FCSTD DOCUMENT  (FreeCAD 0.14R3703 (Git))
Label: hullsSt
License: CC-BY 3.0
LicenseURL: http://creativecommons.org/licenses/by/3.0/
objects: Sketcher::SketchObject×7
note: 7 computed .brp shape members not serialized (recipe doc carries the construction recipe); baked Part::Feature solids carry a one-line shape summary decoded from their .brp

FEATURE [Sketcher::SketchObject] Sketch  label="stemline"
  Placement = pos=(0,0,0) rot=(0.57735,0.57735,0.57735;2.0944rad)
  sketch-geometry (3):
    g0: LineSegment StartX=0 StartY=0 StartZ=0 EndX=25.8227 EndY=11.1446 EndZ=0
    g1: LineSegment StartX=25.8227 StartY=11.1446 StartZ=0 EndX=44.3064 EndY=29.9 EndZ=0
    g2: LineSegment StartX=44.3064 StartY=29.9 StartZ=0 EndX=51.3737 EndY=60.6155 EndZ=0
  constraints (2):
    c: Coincident(g0,g1)
    c: Coincident(g1,g2)
FEATURE [Sketcher::SketchObject] Sketch001  label="cs1"
  Placement = pos=(0,0,0) rot=(1,0,0;1.5708rad)
  sketch-geometry (3):
    g0: LineSegment StartX=0 StartY=0 StartZ=0 EndX=25.0073 EndY=8.15455 EndZ=0
    g1: LineSegment StartX=25.0073 StartY=8.15455 StartZ=0 EndX=38.3264 EndY=24.1918 EndZ=0
    g2: LineSegment StartX=38.3264 StartY=24.1918 StartZ=0 EndX=44.3064 EndY=47.2964 EndZ=0
  constraints (2):
    c: Coincident(g0,g1)
    c: Coincident(g1,g2)
FEATURE [Sketcher::SketchObject] Sketch002  label="cs2"
  Placement = pos=(0,-20,0) rot=(1,0,0;1.5708rad)
  sketch-geometry (3):
    g0: LineSegment StartX=0 StartY=0 StartZ=0 EndX=25.0073 EndY=8.15455 EndZ=0
    g1: LineSegment StartX=25.0073 StartY=8.15455 StartZ=0 EndX=38.3264 EndY=24.1918 EndZ=0
    g2: LineSegment StartX=38.3264 StartY=24.1918 StartZ=0 EndX=44.3064 EndY=47.2964 EndZ=0
  constraints (2):
    c: Coincident(g0,g1)
    c: Coincident(g1,g2)
FEATURE [Sketcher::SketchObject] Sketch004  label="transomXY"
  Placement = pos=(0,-60,0) rot=(0,0,1;0rad)
  sketch-geometry (3):
    g0: LineSegment StartX=-0.069336 StartY=-20.4675 StartZ=0 EndX=25.0103 EndY=-20.3102 EndZ=0
    g1: LineSegment StartX=25.0103 StartY=-20.3102 StartZ=0 EndX=38.297 EndY=-20.2316 EndZ=0
    g2: LineSegment StartX=38.297 StartY=-20.2316 StartZ=0 EndX=44.3064 EndY=-20.1146 EndZ=0
  constraints (2):
    c: Coincident(g0,g1)
    c: Coincident(g1,g2)
FEATURE [Sketcher::SketchObject] Sketch005  label="cs3"
  Placement = pos=(0,-40,0) rot=(1,0,0;1.5708rad)
  sketch-geometry (3):
    g0: LineSegment StartX=0 StartY=0 StartZ=0 EndX=25.0073 EndY=8.15455 EndZ=0
    g1: LineSegment StartX=25.0073 StartY=8.15455 StartZ=0 EndX=38.3264 EndY=24.1918 EndZ=0
    g2: LineSegment StartX=38.3264 StartY=24.1918 StartZ=0 EndX=44.3064 EndY=47.2964 EndZ=0
  constraints (2):
    c: Coincident(g0,g1)
    c: Coincident(g1,g2)
FEATURE [Sketcher::SketchObject] Sketch006  label="cs4"
  Placement = pos=(0,-60,0) rot=(1,0,0;1.5708rad)
  sketch-geometry (3):
    g0: LineSegment StartX=0 StartY=0 StartZ=0 EndX=25.0073 EndY=8.15455 EndZ=0
    g1: LineSegment StartX=25.0073 StartY=8.15455 StartZ=0 EndX=38.3264 EndY=24.1918 EndZ=0
    g2: LineSegment StartX=38.3264 StartY=24.1918 StartZ=0 EndX=44.3064 EndY=47.2964 EndZ=0
  constraints (2):
    c: Coincident(g0,g1)
    c: Coincident(g1,g2)
FEATURE [Sketcher::SketchObject] Sketch007  label="cs5"
  Placement = pos=(0,-80,0) rot=(1,0,0;1.5708rad)
  sketch-geometry (3):
    g0: LineSegment StartX=0 StartY=0 StartZ=0 EndX=25.0073 EndY=8.15455 EndZ=0
    g1: LineSegment StartX=25.0073 StartY=8.15455 StartZ=0 EndX=38.3264 EndY=24.1918 EndZ=0
    g2: LineSegment StartX=38.3264 StartY=24.1918 StartZ=0 EndX=44.3064 EndY=47.2964 EndZ=0
  constraints (2):
    c: Coincident(g0,g1)
    c: Coincident(g1,g2)
